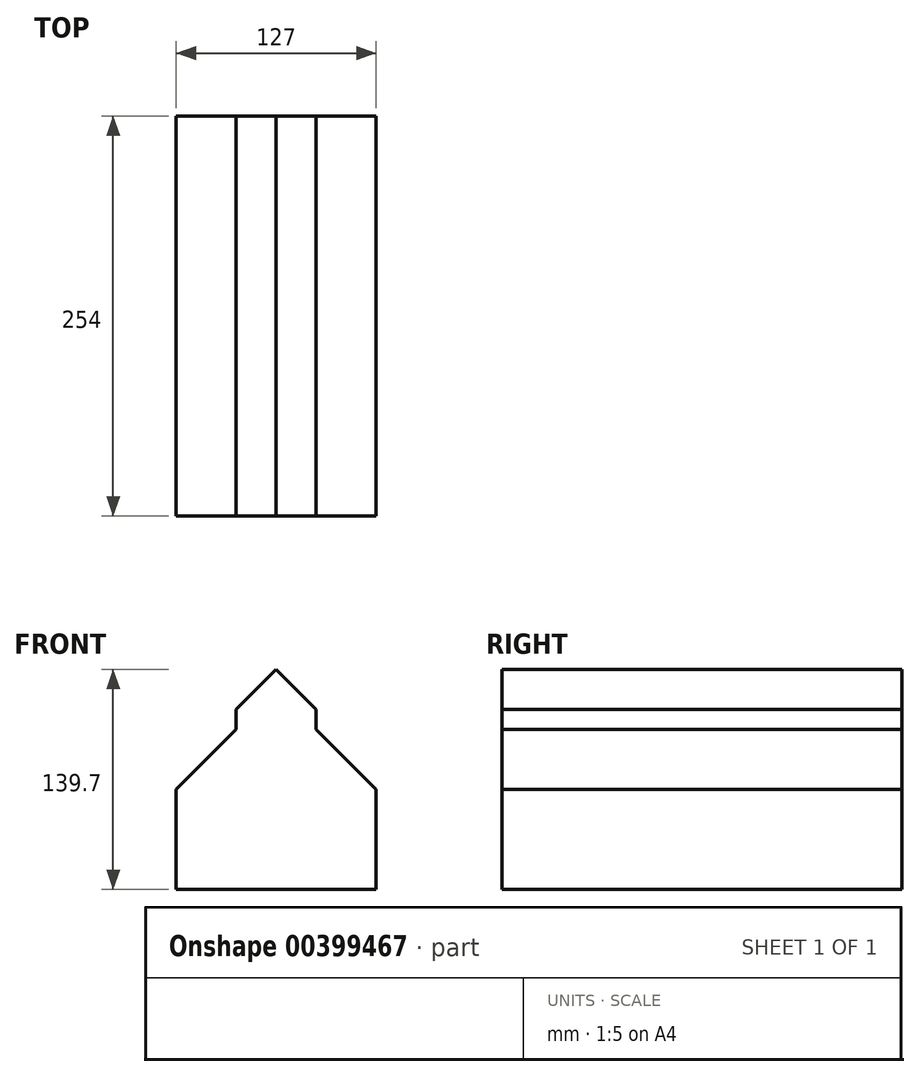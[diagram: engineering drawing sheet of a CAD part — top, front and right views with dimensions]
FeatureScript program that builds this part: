
annotation { "Feature Type Name" : "Feature", "Feature Type Description" : "" }
export const myFeature = defineFeature(function(context is Context, id is Id, definition is map)
    precondition{}
    {
        {
            var Q0;
            Q0=qCreatedBy(makeId("Front.planeOp"),FACE);
            var sketch = newSketch(context, id + "F0", { "sketchPlane" : qUnion([Q0])});
            skLineSegment(sketch, "E0.bottom", {"start": v(0, 0) * mm, "end": v(127, 0) * mm});
            skLineSegment(sketch, "E0.top", {"start": v(0, 101.6) * mm, "end": v(127, 101.6) * mm});
            skLineSegment(sketch, "E0.left", {"start": v(0, 0) * mm, "end": v(0, 101.6) * mm});
            skLineSegment(sketch, "E0.right", {"start": v(127, 0) * mm, "end": v(127, 101.6) * mm});
            skSolve(sketch);
        }
        {
            var Q0;
            Q0=makeQuery(id+"F0.imprint","IMPRINT",FACE,{"disambiguationData":[TD([[makeQuery(id+"F0.imprint","IMPRINT",EDGE,{"derivedFrom":sQuery(id+"F0.wireOp",EDGE,"E0.bottom")}),1.0]])]});
            extrude(context, id + "F1", {"entities" : qUnion([Q0]), "depth" : 254 * mm});
        }
        {
            var Q0;
            Q0=makeQuery(id+"F1.opExtrude","SWEPT_EDGE",EDGE,{"disambiguationData":[OSD([sQuery(id+"F0.wireOp",EDGE,"E0.top"),sQuery(id+"F0.wireOp",EDGE,"E0.right")])]});
            var Q1;
            Q1=makeQuery(id+"F1.opExtrude","SWEPT_EDGE",EDGE,{"disambiguationData":[OSD([sQuery(id+"F0.wireOp",EDGE,"E0.top"),sQuery(id+"F0.wireOp",EDGE,"E0.left")])]});
            chamfer(context, id + "F2", {"entities" : qUnion([Q0, Q1]), "width" : 38.1 * mm, "tangentPropagation" : true});
        }
        {
            var Q0;
            Q0=makeQuery(id+"F1.opExtrude","SWEPT_FACE",FACE,{"disambiguationData":[OSD([sQuery(id+"F0.wireOp",EDGE,"E0.top")])]});
            var sketch = newSketch(context, id + "F3", { "sketchPlane" : qUnion([Q0])});
            skLineSegment(sketch, "E1.bottom", {"start": v(38.1, -254) * mm, "end": v(88.9, -254) * mm});
            skLineSegment(sketch, "E1.top", {"start": v(38.1, 0) * mm, "end": v(88.9, 0) * mm});
            skLineSegment(sketch, "E1.left", {"start": v(38.1, -254) * mm, "end": v(38.1, 0) * mm});
            skLineSegment(sketch, "E1.right", {"start": v(88.9, -254) * mm, "end": v(88.9, 0) * mm});
            skSolve(sketch);
        }
        {
            var Q0;
            Q0=makeQuery(id+"F3.imprint","IMPRINT",FACE,{"disambiguationData":[TD([[makeQuery(id+"F3.imprint","IMPRINT",EDGE,{"derivedFrom":sQuery(id+"F3.wireOp",EDGE,"E1.bottom")}),1.0]])]});
            extrude(context, id + "F4", {"entities" : qUnion([Q0]), "operationType" : NewBodyOperationType.ADD, "depth" : 38.1 * mm});
        }
        {
            var Q0;
            Q0=makeQuery(id+"F4.opExtrude","CAP_EDGE",EDGE,{"disambiguationData":[OSD([sQuery(id+"F3.wireOp",EDGE,"E1.left")])],"isStart":false});
            var Q1;
            Q1=makeQuery(id+"F4.opExtrude","CAP_EDGE",EDGE,{"disambiguationData":[OSD([sQuery(id+"F3.wireOp",EDGE,"E1.right")])],"isStart":false});
            chamfer(context, id + "F5", {"entities" : qUnion([Q0, Q1]), "width" : 25.4 * mm, "tangentPropagation" : true});
        }
    });
